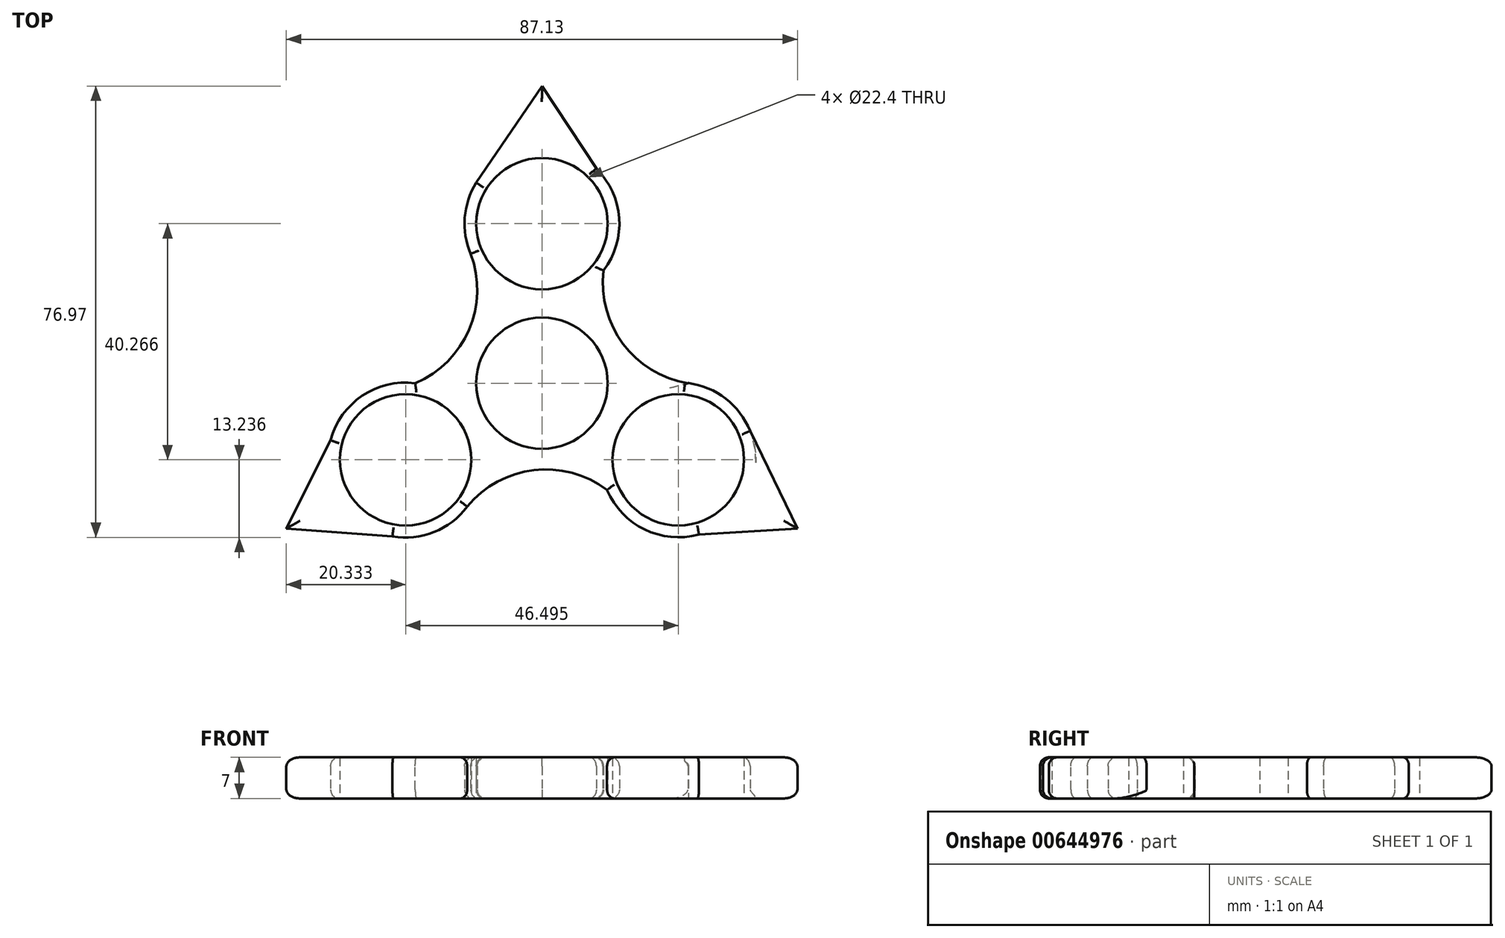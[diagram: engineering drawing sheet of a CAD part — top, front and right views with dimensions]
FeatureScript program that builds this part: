
annotation { "Feature Type Name" : "Feature", "Feature Type Description" : "" }
export const myFeature = defineFeature(function(context is Context, id is Id, definition is map)
    precondition{}
    {
        {
            var Q0;
            Q0=qCreatedBy(makeId("Top.planeOp"),FACE);
            var sketch = newSketch(context, id + "F0", { "sketchPlane" : qUnion([Q0])});
            skCircle(sketch, "E0", {"center": v(0, 0) * mm, "radius": 11.2 * mm});
            skCircle(sketch, "E1", {"center": v(0, 27.2) * mm, "radius": 11.2 * mm});
            skArc(sketch, "E2", {"start": v(10.51, 19.22) * mm, "mid": v(13.17, 28.14) * mm, "end": v(9.27, 36.6) * mm});
            skLineSegment(sketch, "E3.1.0", {"start": v(-12.74, -21.05) * mm, "end": v(-12.74, -21.05) * mm});
            skCircle(sketch, "E3.1.1", {"center": v(-23.25, -13.06) * mm, "radius": 11.2 * mm});
            skArc(sketch, "E3.2.0", {"start": v(11.1, -18.2) * mm, "mid": v(33.75, -21.06) * mm, "end": v(24.97, 0.02) * mm});
            skCircle(sketch, "E3.2.1", {"center": v(23.25, -13.06) * mm, "radius": 11.2 * mm});
            skPoint(sketch, "E3.center", {"position": v(0, 0.36) * mm});
            skArc(sketch, "E4", {"start": v(-21.6, 0) * mm, "mid": v(-12.44, 9.12) * mm, "end": v(-12.16, 22.06) * mm});
            skArc(sketch, "E5.1.0", {"start": v(11.1, -18.2) * mm, "mid": v(-1.4, -14.82) * mm, "end": v(-12.74, -21.05) * mm});
            skArc(sketch, "E5.2.0", {"start": v(10.51, 19.22) * mm, "mid": v(13.82, 6.7) * mm, "end": v(24.89, 0) * mm});
            skPoint(sketch, "E5.center", {"position": v(0, 0.34) * mm});
            skLineSegment(sketch, "E6", {"start": v(-11.2, 34.18) * mm, "end": v(0, 50.67) * mm});
            skLineSegment(sketch, "E7", {"start": v(0, 50.67) * mm, "end": v(9.27, 36.6) * mm});
            skLineSegment(sketch, "E8.1.0", {"start": v(-43.58, -24.78) * mm, "end": v(-36.03, -9.72) * mm});
            skLineSegment(sketch, "E8.1.1", {"start": v(-23.7, -26.24) * mm, "end": v(-43.58, -24.78) * mm});
            skLineSegment(sketch, "E8.2.0", {"start": v(43.55, -24.8) * mm, "end": v(26.76, -25.79) * mm});
            skLineSegment(sketch, "E8.2.1", {"start": v(35.49, -8.13) * mm, "end": v(43.55, -24.8) * mm});
            skPoint(sketch, "E8.center", {"position": v(-0.01, 0.36) * mm});
            skArc(sketch, "E9.1.0", {"start": v(-21.6, 0) * mm, "mid": v(-30.65, -2.15) * mm, "end": v(-36.03, -9.72) * mm});
            skArc(sketch, "E10.trimOffspring", {"start": v(-25.5, -26.1) * mm, "mid": v(-18.4, -25.37) * mm, "end": v(-12.74, -21.05) * mm});
            skArc(sketch, "E11.trimOffspring", {"start": v(-10.61, 35.05) * mm, "mid": v(-13.1, 28.76) * mm, "end": v(-12.16, 22.06) * mm});
            skPoint(sketch, "E12.orphan", {"position": v(26.73, -25.79) * mm});
            skPoint(sketch, "E13.orphan", {"position": v(34.87, -6.85) * mm});
            skLineSegment(sketch, "E14", {"start": v(24.89, 0) * mm, "end": v(24.97, 0.02) * mm});
            skPoint(sketch, "E15.orphan", {"position": v(27.06, -26.33) * mm});
            skPoint(sketch, "E16.orphan", {"position": v(-21.9, -0.5) * mm});
            skSolve(sketch);
        }
        {
            var Q0;
            Q0=makeQuery(id+"F0.imprint","IMPRINT",FACE,{"disambiguationData":[TD([[makeQuery(id+"F0.imprint","IMPRINT",EDGE,{"derivedFrom":sQuery(id+"F0.wireOp",EDGE,"E0")}),-1.0]])]});
            var Q1;
            {var subQ0=sQuery(id+"F0.wireOp",EDGE,"E8.2.0");Q1=makeQuery(id+"F0.imprint","IMPRINT",FACE,{"disambiguationData":[TD([[makeQuery(id+"F0.imprint","IMPRINT",EDGE,{"derivedFrom":subQ0}),-1.0]])]});}
            extrude(context, id + "F1", {"entities" : qUnion([Q0, Q1]), "depth" : 7 * mm, "offsetDistance" : 25 * mm});
        }
        {
            var Q0;
            Q0=makeQuery(id+"F1.opExtrude","CAP_EDGE",EDGE,{"disambiguationData":[OSD([sQuery(id+"F0.wireOp",EDGE,"E5.1.0")])],"isStart":false});
            var Q1;
            Q1=makeQuery(id+"F1.opExtrude","CAP_EDGE",EDGE,{"disambiguationData":[OSD([sQuery(id+"F0.wireOp",EDGE,"E10.trimOffspring")])],"isStart":false});
            var Q2;
            Q2=makeQuery(id+"F1.opExtrude","CAP_EDGE",EDGE,{"disambiguationData":[OSD([sQuery(id+"F0.wireOp",EDGE,"E8.1.1")])],"isStart":false});
            var Q3;
            Q3=makeQuery(id+"F1.opExtrude","CAP_EDGE",EDGE,{"disambiguationData":[OSD([sQuery(id+"F0.wireOp",EDGE,"E8.1.0")])],"isStart":false});
            var Q4;
            Q4=makeQuery(id+"F1.opExtrude","CAP_EDGE",EDGE,{"disambiguationData":[OSD([sQuery(id+"F0.wireOp",EDGE,"E9.1.0")])],"isStart":false});
            var Q5;
            {var subQ0=sQuery(id+"F0.wireOp",EDGE,"E3.2.0");Q5=makeQuery(id+"F1.opExtrude","CAP_EDGE",EDGE,{"disambiguationData":[OSD([subQ0]),TDD([makeQuery(id+"F0.imprint","IMPRINT",EDGE,{"disambiguationData":[TD([[makeQuery(id+"F0.imprint","INTERSECT",VERTEX,{"derivedFrom":[subQ0,sQuery(id+"F0.wireOp",EDGE,"E5.1.0")]}),-1.0]])],"derivedFrom":subQ0})])],"isStart":false});}
            var Q6;
            Q6=makeQuery(id+"F1.opExtrude","CAP_EDGE",EDGE,{"disambiguationData":[OSD([sQuery(id+"F0.wireOp",EDGE,"E2")])],"isStart":false});
            var Q7;
            Q7=makeQuery(id+"F1.opExtrude","CAP_EDGE",EDGE,{"disambiguationData":[OSD([sQuery(id+"F0.wireOp",EDGE,"E11.trimOffspring")])],"isStart":false});
            var Q8;
            Q8=makeQuery(id+"F1.opExtrude","CAP_EDGE",EDGE,{"disambiguationData":[OSD([sQuery(id+"F0.wireOp",EDGE,"E6")])],"isStart":false});
            var Q9;
            Q9=makeQuery(id+"F1.opExtrude","CAP_EDGE",EDGE,{"disambiguationData":[OSD([sQuery(id+"F0.wireOp",EDGE,"E7")])],"isStart":false});
            var Q10;
            Q10=makeQuery(id+"F1.opExtrude","CAP_EDGE",EDGE,{"disambiguationData":[OSD([sQuery(id+"F0.wireOp",EDGE,"E8.2.0")])],"isStart":false});
            var Q11;
            Q11=makeQuery(id+"F1.opExtrude","CAP_EDGE",EDGE,{"disambiguationData":[OSD([sQuery(id+"F0.wireOp",EDGE,"E5.2.0")])],"isStart":false});
            var Q12;
            Q12=makeQuery(id+"F1.opExtrude","CAP_EDGE",EDGE,{"disambiguationData":[OSD([sQuery(id+"F0.wireOp",EDGE,"E4")])],"isStart":false});
            var Q13;
            Q13=makeQuery(id+"F1.opExtrude","CAP_EDGE",EDGE,{"disambiguationData":[OSD([sQuery(id+"F0.wireOp",EDGE,"E8.2.1")])],"isStart":false});
            fillet(context, id + "F2", {"entities" : qUnion([Q0, Q1, Q2, Q3, Q4, Q5, Q6, Q7, Q8, Q9, Q10, Q11, Q12, Q13]), "radius" : 1.5 * mm, "tangentPropagation" : true, "allowEdgeOverflow" : false});
        }
        {
            var Q0;
            Q0=makeQuery(id+"F1.opExtrude","CAP_EDGE",EDGE,{"disambiguationData":[OSD([sQuery(id+"F0.wireOp",EDGE,"E4")])],"isStart":true});
            var Q1;
            Q1=makeQuery(id+"F1.opExtrude","CAP_EDGE",EDGE,{"disambiguationData":[OSD([sQuery(id+"F0.wireOp",EDGE,"E9.1.0")])],"isStart":true});
            var Q2;
            Q2=makeQuery(id+"F1.opExtrude","CAP_EDGE",EDGE,{"disambiguationData":[OSD([sQuery(id+"F0.wireOp",EDGE,"E8.1.0")])],"isStart":true});
            var Q3;
            Q3=makeQuery(id+"F1.opExtrude","CAP_EDGE",EDGE,{"disambiguationData":[OSD([sQuery(id+"F0.wireOp",EDGE,"E8.1.1")])],"isStart":true});
            var Q4;
            Q4=makeQuery(id+"F1.opExtrude","CAP_EDGE",EDGE,{"disambiguationData":[OSD([sQuery(id+"F0.wireOp",EDGE,"E10.trimOffspring")])],"isStart":true});
            var Q5;
            Q5=makeQuery(id+"F1.opExtrude","CAP_EDGE",EDGE,{"disambiguationData":[OSD([sQuery(id+"F0.wireOp",EDGE,"E5.1.0")])],"isStart":true});
            var Q6;
            {var subQ0=sQuery(id+"F0.wireOp",EDGE,"E3.2.0");Q6=makeQuery(id+"F1.opExtrude","CAP_EDGE",EDGE,{"disambiguationData":[OSD([subQ0]),TDD([makeQuery(id+"F0.imprint","IMPRINT",EDGE,{"disambiguationData":[TD([[makeQuery(id+"F0.imprint","INTERSECT",VERTEX,{"derivedFrom":[subQ0,sQuery(id+"F0.wireOp",EDGE,"E5.1.0")]}),-1.0]])],"derivedFrom":subQ0})])],"isStart":true});}
            var Q7;
            Q7=makeQuery(id+"F1.opExtrude","CAP_EDGE",EDGE,{"disambiguationData":[OSD([sQuery(id+"F0.wireOp",EDGE,"E5.2.0")])],"isStart":true});
            var Q8;
            Q8=makeQuery(id+"F1.opExtrude","CAP_EDGE",EDGE,{"disambiguationData":[OSD([sQuery(id+"F0.wireOp",EDGE,"E2")])],"isStart":true});
            var Q9;
            Q9=makeQuery(id+"F1.opExtrude","CAP_EDGE",EDGE,{"disambiguationData":[OSD([sQuery(id+"F0.wireOp",EDGE,"E7")])],"isStart":true});
            var Q10;
            Q10=makeQuery(id+"F1.opExtrude","CAP_EDGE",EDGE,{"disambiguationData":[OSD([sQuery(id+"F0.wireOp",EDGE,"E6")])],"isStart":true});
            var Q11;
            Q11=makeQuery(id+"F1.opExtrude","CAP_EDGE",EDGE,{"disambiguationData":[OSD([sQuery(id+"F0.wireOp",EDGE,"E11.trimOffspring")])],"isStart":true});
            var Q12;
            Q12=makeQuery(id+"F1.opExtrude","CAP_EDGE",EDGE,{"disambiguationData":[OSD([sQuery(id+"F0.wireOp",EDGE,"E8.2.1")])],"isStart":true});
            var Q13;
            Q13=makeQuery(id+"F1.opExtrude","CAP_EDGE",EDGE,{"disambiguationData":[OSD([sQuery(id+"F0.wireOp",EDGE,"E8.2.0")])],"isStart":true});
            var Q14;
            {var subQ0=sQuery(id+"F0.wireOp",EDGE,"E3.2.0");Q14=makeQuery(id+"F1.opExtrude","CAP_EDGE",EDGE,{"disambiguationData":[OSD([subQ0]),TDD([makeQuery(id+"F0.imprint","IMPRINT",EDGE,{"disambiguationData":[TD([[makeQuery(id+"F0.imprint","INTERSECT",VERTEX,{"derivedFrom":[subQ0,sQuery(id+"F0.wireOp",EDGE,"E14")]}),1.0]])],"derivedFrom":subQ0})])],"isStart":false});}
            fillet(context, id + "F3", {"entities" : qUnion([Q0, Q1, Q2, Q3, Q4, Q5, Q6, Q7, Q8, Q9, Q10, Q11, Q12, Q13, Q14]), "radius" : 1.5 * mm, "tangentPropagation" : true, "allowEdgeOverflow" : false});
        }
    });
